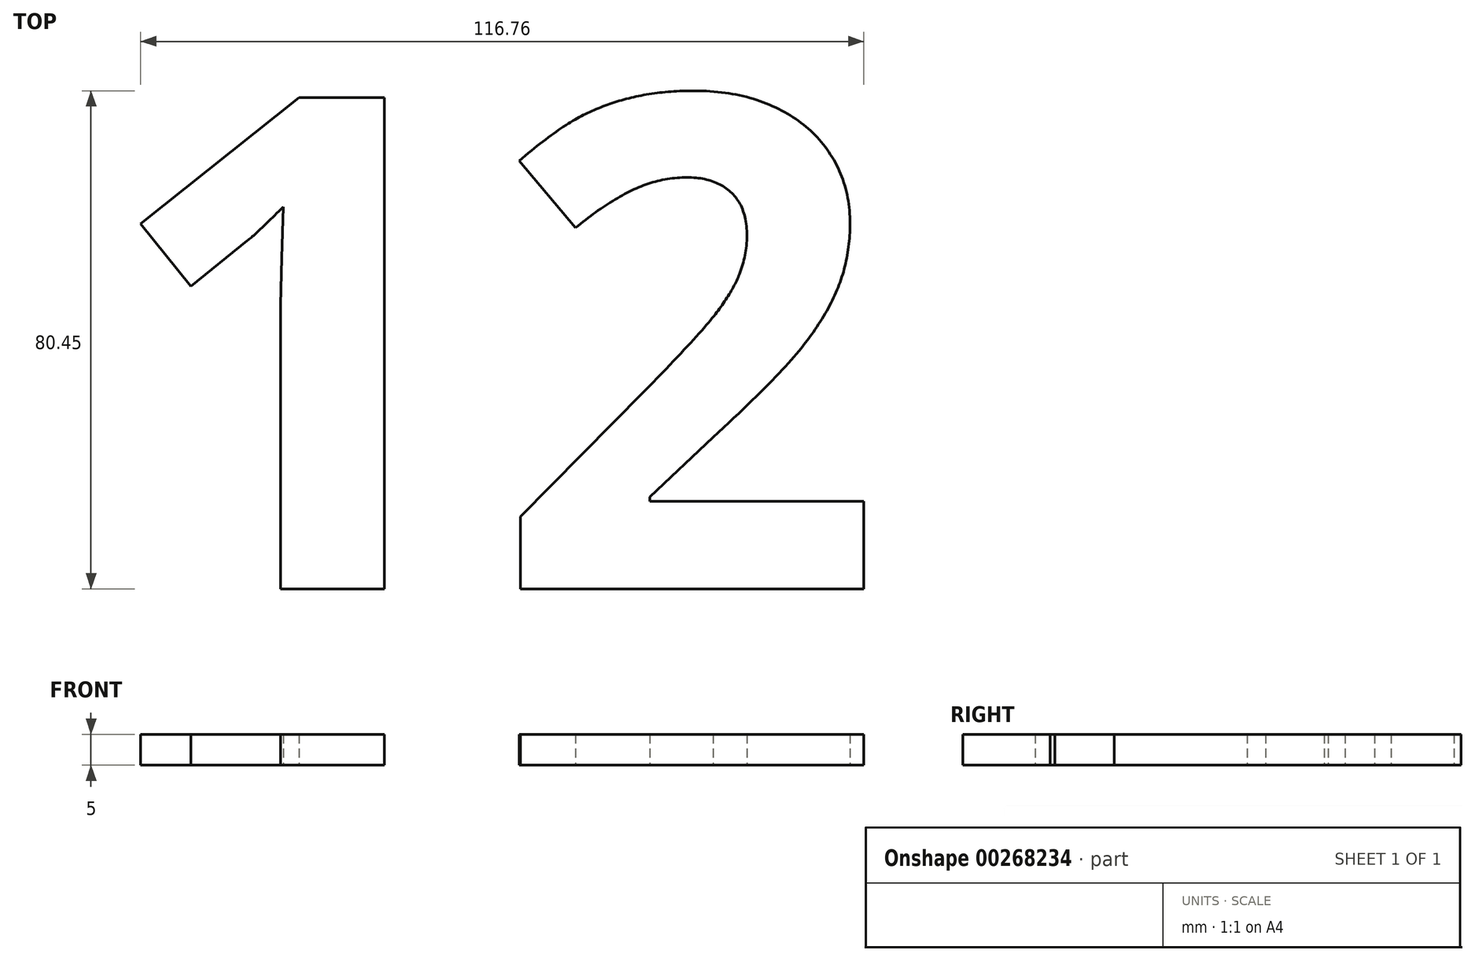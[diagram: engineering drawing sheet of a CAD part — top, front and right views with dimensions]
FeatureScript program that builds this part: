
annotation { "Feature Type Name" : "Feature", "Feature Type Description" : "" }
export const myFeature = defineFeature(function(context is Context, id is Id, definition is map)
    precondition{}
    {
        {
            var Q0;
            Q0=qCreatedBy(makeId("Top.planeOp"),FACE);
            var sketch = newSketch(context, id + "F0", { "sketchPlane" : qUnion([Q0])});
            skText(sketch, "E0", { "text": "12", "fontName": "OpenSans-Bold.ttf"});
            const initialGuessF0  = {"E0": [-0.07116, -0.05043, 1, 0, 0.08]};
            skSetInitialGuess(sketch, initialGuessF0);
            skSolve(sketch);
        }
        {
            var Q0;
            Q0=makeQuery(id+"F0.imprint","IMPRINT",FACE,{"disambiguationData":[TD([[makeQuery(id+"F0.imprint","IMPRINT",EDGE,{"derivedFrom":sQuery(id+"F0.wireOp",EDGE,"E0.sketch_text.stroke-0")}),-1.0]])]});
            var Q1;
            Q1=makeQuery(id+"F0.imprint","IMPRINT",FACE,{"disambiguationData":[TD([[makeQuery(id+"F0.imprint","IMPRINT",EDGE,{"derivedFrom":sQuery(id+"F0.wireOp",EDGE,"E0.sketch_text.stroke-10")}),-1.0]])]});
            extrude(context, id + "F1", {"entities" : qUnion([Q0, Q1]), "depth" : 5 * mm});
        }
    });
